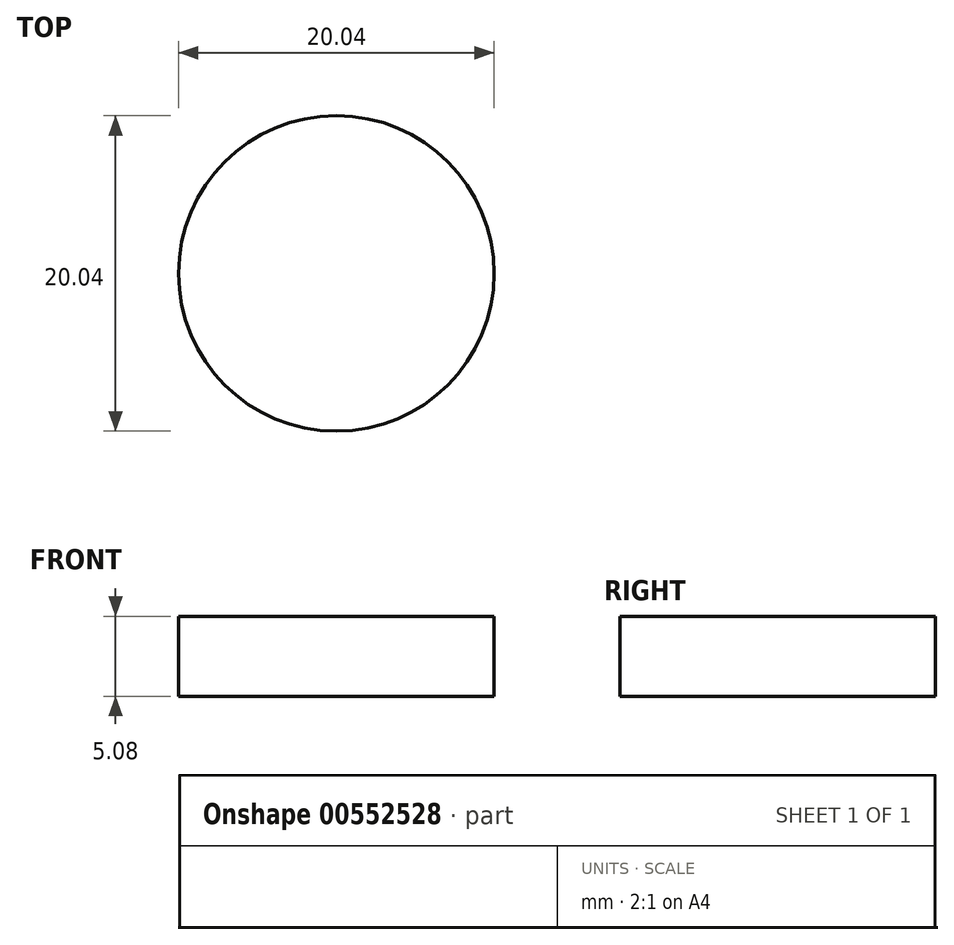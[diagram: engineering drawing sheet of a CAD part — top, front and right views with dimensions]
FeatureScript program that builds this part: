
annotation { "Feature Type Name" : "Feature", "Feature Type Description" : "" }
export const myFeature = defineFeature(function(context is Context, id is Id, definition is map)
    precondition{}
    {
        {
            var Q0;
            Q0=qCreatedBy(makeId("Top.planeOp"),FACE);
            var sketch = newSketch(context, id + "F0", { "sketchPlane" : qUnion([Q0])});
            skCircle(sketch, "E0", {"center": v(0, 0) * mm, "radius": 10.02 * mm});
            skLineSegment(sketch, "E1", {"start": v(-10.02, 0) * mm, "end": v(-31.7, 20.41) * mm});
            skLineSegment(sketch, "E2", {"start": v(-31.7, 20.41) * mm, "end": v(-10.02, 0) * mm});
            skArc(sketch, "E3", {"start": v(-19.2, 28.23) * mm, "mid": v(-30.51, 32.42) * mm, "end": v(-31.7, 20.41) * mm});
            skLineSegment(sketch, "E4", {"start": v(-19.2, 28.23) * mm, "end": v(0, 10.02) * mm});
            skLineSegment(sketch, "E5", {"start": v(0, 10.02) * mm, "end": v(16.81, 28.23) * mm});
            skLineSegment(sketch, "E6", {"start": v(16.81, 28.23) * mm, "end": v(0, 10.02) * mm});
            skArc(sketch, "E7", {"start": v(30.25, 21.38) * mm, "mid": v(27.46, 32.51) * mm, "end": v(16.81, 28.23) * mm});
            skLineSegment(sketch, "E8", {"start": v(30.25, 21.38) * mm, "end": v(10.02, 0) * mm});
            skLineSegment(sketch, "E9", {"start": v(10.02, 0) * mm, "end": v(30.25, 21.38) * mm});
            skSolve(sketch);
        }
        {
            var Q0;
            Q0=qCreatedBy(makeId("Top.planeOp"),FACE);
            var sketch = newSketch(context, id + "F1", { "sketchPlane" : qUnion([Q0])});
            skLineSegment(sketch, "E10", {"start": v(11.14, 0) * mm, "end": v(26.4, -25.58) * mm});
            skArc(sketch, "E11", {"start": v(13.96, -34.31) * mm, "mid": v(24.23, -35.71) * mm, "end": v(26.4, -25.58) * mm});
            skLineSegment(sketch, "E12", {"start": v(13.96, -34.31) * mm, "end": v(0, -10.08) * mm});
            skLineSegment(sketch, "E13", {"start": v(0, -10.08) * mm, "end": v(13.96, -34.31) * mm});
            skSolve(sketch);
        }
        {
            var Q0;
            Q0=qCreatedBy(makeId("Top.planeOp"),FACE);
            var sketch = newSketch(context, id + "F2", { "sketchPlane" : qUnion([Q0])});
            skLineSegment(sketch, "E14", {"start": v(-9.28, 0) * mm, "end": v(-28.08, -23.1) * mm});
            skLineSegment(sketch, "E15", {"start": v(-28.08, -23.1) * mm, "end": v(-9.28, 0) * mm});
            skArc(sketch, "E16", {"start": v(-28.08, -23.1) * mm, "mid": v(-25.13, -34.93) * mm, "end": v(-14.6, -28.79) * mm});
            skLineSegment(sketch, "E17", {"start": v(-14.6, -28.79) * mm, "end": v(0, -10.85) * mm});
            skLineSegment(sketch, "E18", {"start": v(0, -10.85) * mm, "end": v(-14.6, -28.79) * mm});
            skSolve(sketch);
        }
        {
            var Q0;
            Q0=sQuery(id+"F2.wireOp",EDGE,"E15");
            var Q1;
            Q1=sQuery(id+"F2.wireOp",EDGE,"E18");
            var Q2;
            Q2=sQuery(id+"F2.wireOp",EDGE,"E16");
            var Q3;
            Q3=sQuery(id+"F1.wireOp",EDGE,"E13");
            var Q4;
            Q4=sQuery(id+"F1.wireOp",EDGE,"E11");
            var Q5;
            Q5=sQuery(id+"F1.wireOp",EDGE,"E10");
            extrude(context, id + "F3", {"bodyType" : ToolBodyType.SURFACE, "surfaceEntities" : qUnion([Q0, Q1, Q2, Q3, Q4, Q5]), "depth" : 5.08 * mm, "offsetDistance" : 25.4 * mm});
        }
        {
            var Q0;
            {var subQ0=sQuery(id+"F0.wireOp",EDGE,"E6");Q0=makeQuery(id+"F0.imprint","IMPRINT",FACE,{"disambiguationData":[TD([[makeQuery(id+"F0.imprint","IMPRINT",EDGE,{"derivedFrom":subQ0}),1.0]])]});}
            var Q1;
            {var subQ0=sQuery(id+"F0.wireOp",EDGE,"E2");Q1=makeQuery(id+"F0.imprint","IMPRINT",FACE,{"disambiguationData":[TD([[makeQuery(id+"F0.imprint","IMPRINT",EDGE,{"derivedFrom":subQ0}),1.0]])]});}
            var Q2;
            {var subQ0=sQuery(id+"F0.wireOp",EDGE,"E0");var subQ3=makeQuery(id+"F0.imprint","INTERSECT",VERTEX,{"derivedFrom":[subQ0,sQuery(id+"F0.wireOp",EDGE,"E2")]});Q2=makeQuery(id+"F0.imprint","IMPRINT",FACE,{"disambiguationData":[TD([[makeQuery(id+"F0.imprint","IMPRINT",EDGE,{"disambiguationData":[TD([[subQ3,-1.0]])],"derivedFrom":subQ0}),1.0]])]});}
            extrude(context, id + "F4", {"entities" : qUnion([Q0, Q1, Q2]), "depth" : 5.08 * mm, "offsetDistance" : 25.4 * mm});
        }
    });
